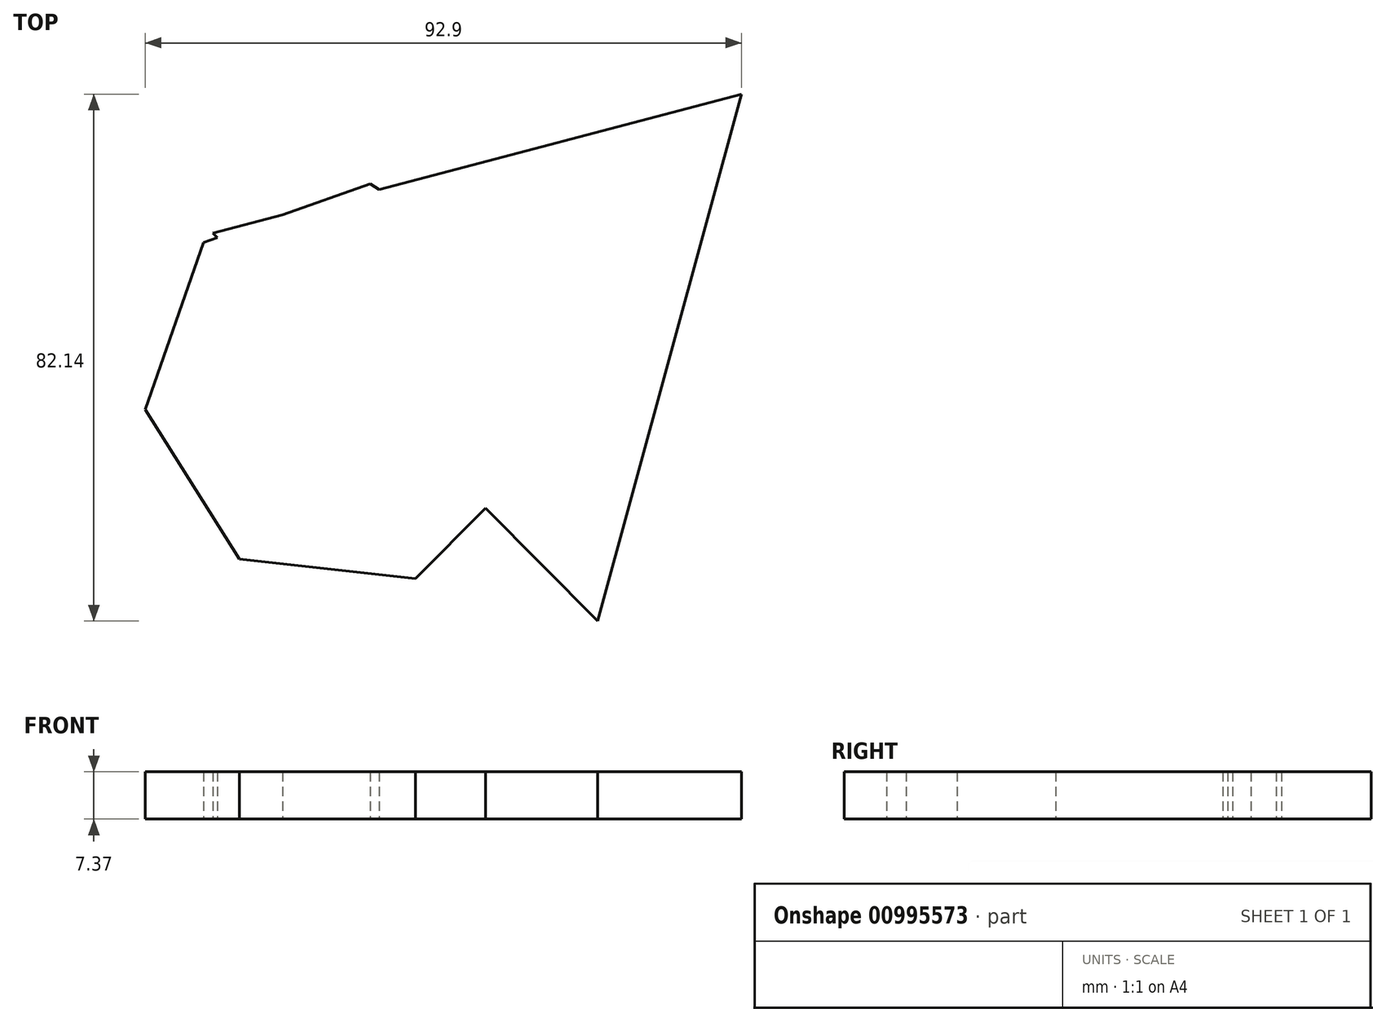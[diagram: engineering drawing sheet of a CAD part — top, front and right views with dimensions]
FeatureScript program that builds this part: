
annotation { "Feature Type Name" : "Feature", "Feature Type Description" : "" }
export const myFeature = defineFeature(function(context is Context, id is Id, definition is map)
    precondition{}
    {
        {
            var Q0;
            Q0=qCreatedBy(makeId("Top.planeOp"),FACE);
            var sketch = newSketch(context, id + "F0", { "sketchPlane" : qUnion([Q0])});
            skCircle(sketch, "E0.cCircle", {"center": v(10.83, -31.06) * mm, "radius": 28.6 * mm, "construction": true});
            skLineSegment(sketch, "E0.0", {"start": v(14.34, 0.5) * mm, "end": v(37.7, -14.13) * mm});
            skLineSegment(sketch, "E0.1", {"start": v(37.7, -14.13) * mm, "end": v(40.82, -41.5) * mm});
            skLineSegment(sketch, "E0.2", {"start": v(40.82, -41.5) * mm, "end": v(21.36, -61.01) * mm});
            skLineSegment(sketch, "E0.3", {"start": v(21.36, -61.01) * mm, "end": v(-6.02, -57.96) * mm});
            skLineSegment(sketch, "E0.4", {"start": v(-6.02, -57.96) * mm, "end": v(-20.72, -34.65) * mm});
            skLineSegment(sketch, "E0.5", {"start": v(-20.72, -34.65) * mm, "end": v(-11.65, -8.63) * mm});
            skLineSegment(sketch, "E0.6", {"start": v(-11.65, -8.63) * mm, "end": v(14.34, 0.5) * mm});
            skPoint(sketch, "E0.0.midPoint", {"position": v(26.02, -6.81) * mm});
            skCircle(sketch, "E1.cCircle", {"center": v(37.26, -20.1) * mm, "radius": 24.58 * mm, "construction": true});
            skLineSegment(sketch, "E1.0", {"start": v(49.76, -67.64) * mm, "end": v(-10.17, -7.15) * mm});
            skLineSegment(sketch, "E1.1", {"start": v(-10.17, -7.15) * mm, "end": v(72.18, 14.5) * mm});
            skLineSegment(sketch, "E1.2", {"start": v(72.18, 14.5) * mm, "end": v(49.76, -67.64) * mm});
            skPoint(sketch, "E1.0.midPoint", {"position": v(19.8, -37.4) * mm});
            skSolve(sketch);
        }
        {
            var Q0;
            Q0 = qSketchRegion(id + "F0", true);
            extrude(context, id + "F1", {"entities" : qUnion([Q0]), "depth" : 7.37 * mm, "offsetDistance" : 25.4 * mm});
        }
    });
